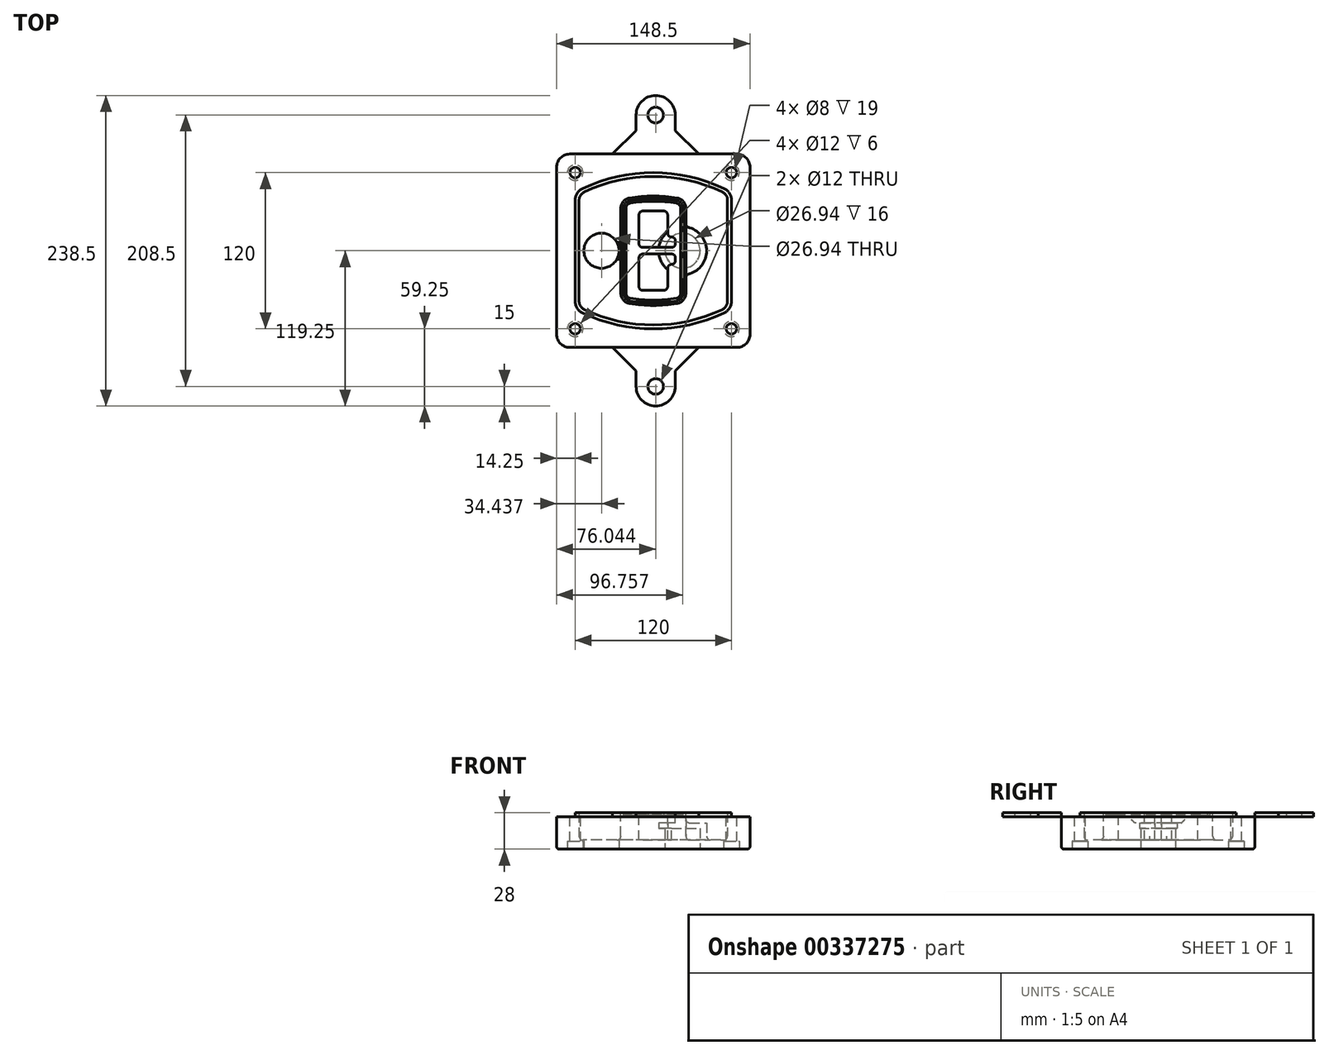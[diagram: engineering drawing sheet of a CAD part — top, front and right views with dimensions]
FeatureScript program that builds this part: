
annotation { "Feature Type Name" : "Feature", "Feature Type Description" : "" }
export const myFeature = defineFeature(function(context is Context, id is Id, definition is map)
    precondition{}
    {
        {
            var Q0;
            Q0=qCreatedBy(makeId("Top.planeOp"),FACE);
            var sketch = newSketch(context, id + "F0", { "sketchPlane" : qUnion([Q0])});
            skPoint(sketch, "E0.rect.middle", {"position": v(0, 0) * mm});
            skLineSegment(sketch, "E1.bottom", {"start": v(-64.25, -74.25) * mm, "end": v(64.25, -74.25) * mm});
            skLineSegment(sketch, "E1.top", {"start": v(-64.25, 74.25) * mm, "end": v(64.25, 74.25) * mm});
            skLineSegment(sketch, "E1.left", {"start": v(-74.25, -64.25) * mm, "end": v(-74.25, 64.25) * mm});
            skLineSegment(sketch, "E1.right", {"start": v(74.25, -64.25) * mm, "end": v(74.25, 64.25) * mm});
            skLineSegment(sketch, "E2", {"start": v(-74.25, 74.25) * mm, "end": v(74.25, -74.25) * mm, "construction": true});
            skLineSegment(sketch, "E3", {"start": v(74.25, 74.25) * mm, "end": v(-74.25, -74.25) * mm, "construction": true});
            skCircle(sketch, "E4", {"center": v(-60, 60) * mm, "radius": 4 * mm});
            skCircle(sketch, "E5", {"center": v(60, 60) * mm, "radius": 4 * mm});
            skCircle(sketch, "E6", {"center": v(60, -60) * mm, "radius": 4 * mm});
            skCircle(sketch, "E7", {"center": v(-60, -60) * mm, "radius": 4 * mm});
            skLineSegment(sketch, "E8", {"start": v(-60, 60) * mm, "end": v(60, 60) * mm, "construction": true});
            skLineSegment(sketch, "E9", {"start": v(60, 60) * mm, "end": v(60, -60) * mm, "construction": true});
            skLineSegment(sketch, "E10", {"start": v(60, -60) * mm, "end": v(-60, -60) * mm, "construction": true});
            skLineSegment(sketch, "E11", {"start": v(-60, -60) * mm, "end": v(-60, 60) * mm, "construction": true});
            skLineSegment(sketch, "E12", {"start": v(-60, 38.83) * mm, "end": v(-60, -38.83) * mm});
            skLineSegment(sketch, "E13", {"start": v(60, 38.83) * mm, "end": v(60, -38.83) * mm});
            skArc(sketch, "E14", {"start": v(54.26, 47.88) * mm, "mid": v(0, 60) * mm, "end": v(-54.26, 47.88) * mm});
            skArc(sketch, "E15", {"start": v(-54.26, -47.88) * mm, "mid": v(0, -60) * mm, "end": v(54.26, -47.88) * mm});
            skLineSegment(sketch, "E16", {"start": v(-60, 0) * mm, "end": v(60, 0) * mm, "construction": true});
            skPoint(sketch, "E17.visualSharp", {"position": v(-60, -45) * mm});
            skArc(sketch, "E17.filletArc", {"start": v(-60, -38.83) * mm, "mid": v(-58.44, -44.2) * mm, "end": v(-54.26, -47.88) * mm});
            skPoint(sketch, "E18.visualSharp", {"position": v(-60, 45) * mm});
            skArc(sketch, "E18.filletArc", {"start": v(-54.26, 47.88) * mm, "mid": v(-58.44, 44.2) * mm, "end": v(-60, 38.83) * mm});
            skPoint(sketch, "E19.visualSharp", {"position": v(60, 45) * mm});
            skArc(sketch, "E19.filletArc", {"start": v(60, 38.83) * mm, "mid": v(58.44, 44.2) * mm, "end": v(54.26, 47.88) * mm});
            skPoint(sketch, "E20.visualSharp", {"position": v(60, -45) * mm});
            skArc(sketch, "E20.filletArc", {"start": v(54.26, -47.88) * mm, "mid": v(58.44, -44.2) * mm, "end": v(60, -38.83) * mm});
            skPoint(sketch, "E21.visualSharp", {"position": v(-74.25, 74.25) * mm});
            skArc(sketch, "E21.filletArc", {"start": v(-64.25, 74.25) * mm, "mid": v(-71.32, 71.32) * mm, "end": v(-74.25, 64.25) * mm});
            skPoint(sketch, "E22.visualSharp", {"position": v(74.25, 74.25) * mm});
            skArc(sketch, "E22.filletArc", {"start": v(74.25, 64.25) * mm, "mid": v(71.32, 71.32) * mm, "end": v(64.25, 74.25) * mm});
            skPoint(sketch, "E23.visualSharp", {"position": v(74.25, -74.25) * mm});
            skArc(sketch, "E23.filletArc", {"start": v(64.25, -74.25) * mm, "mid": v(71.32, -71.32) * mm, "end": v(74.25, -64.25) * mm});
            skPoint(sketch, "E24.visualSharp", {"position": v(-74.25, -74.25) * mm});
            skArc(sketch, "E24.filletArc", {"start": v(-74.25, -64.25) * mm, "mid": v(-71.32, -71.32) * mm, "end": v(-64.25, -74.25) * mm});
            skArc(sketch, "E25.0", {"start": v(57, 38.83) * mm, "mid": v(55.9, 42.58) * mm, "end": v(52.98, 45.17) * mm});
            skLineSegment(sketch, "E25.1", {"start": v(57, 38.83) * mm, "end": v(57, -38.83) * mm});
            skArc(sketch, "E25.2", {"start": v(52.98, -45.17) * mm, "mid": v(55.9, -42.58) * mm, "end": v(57, -38.83) * mm});
            skArc(sketch, "E25.3", {"start": v(-52.98, -45.17) * mm, "mid": v(0, -57) * mm, "end": v(52.98, -45.17) * mm});
            skArc(sketch, "E25.4", {"start": v(-57, -38.83) * mm, "mid": v(-55.9, -42.58) * mm, "end": v(-52.98, -45.17) * mm});
            skArc(sketch, "E25.5", {"start": v(52.98, 45.17) * mm, "mid": v(0, 57) * mm, "end": v(-52.98, 45.17) * mm});
            skLineSegment(sketch, "E25.6", {"start": v(-57, 38.83) * mm, "end": v(-57, -38.83) * mm});
            skArc(sketch, "E25.7", {"start": v(-52.98, 45.17) * mm, "mid": v(-55.9, 42.58) * mm, "end": v(-57, 38.83) * mm});
            skArc(sketch, "E26.0", {"start": v(-55.96, 51.5) * mm, "mid": v(-61.82, 46.33) * mm, "end": v(-64, 38.83) * mm});
            skArc(sketch, "E26.1", {"start": v(55.96, 51.5) * mm, "mid": v(0, 64) * mm, "end": v(-55.96, 51.5) * mm});
            skArc(sketch, "E26.2", {"start": v(64, 38.83) * mm, "mid": v(61.82, 46.33) * mm, "end": v(55.96, 51.5) * mm});
            skLineSegment(sketch, "E26.3", {"start": v(64, 38.83) * mm, "end": v(64, -38.83) * mm});
            skArc(sketch, "E26.4", {"start": v(55.96, -51.5) * mm, "mid": v(61.82, -46.33) * mm, "end": v(64, -38.83) * mm});
            skLineSegment(sketch, "E26.5", {"start": v(-64, 38.83) * mm, "end": v(-64, -38.83) * mm});
            skArc(sketch, "E26.6", {"start": v(-55.96, -51.5) * mm, "mid": v(0, -64) * mm, "end": v(55.96, -51.5) * mm});
            skArc(sketch, "E26.7", {"start": v(-64, -38.83) * mm, "mid": v(-61.82, -46.33) * mm, "end": v(-55.96, -51.5) * mm});
            skSolve(sketch);
        }
        {
            var Q0;
            Q0=makeQuery(id+"F0.imprint","IMPRINT",FACE,{"disambiguationData":[TD([[makeQuery(id+"F0.imprint","IMPRINT",EDGE,{"derivedFrom":sQuery(id+"F0.wireOp",EDGE,"E1.bottom")}),1.0]])]});
            var Q1;
            Q1=makeQuery(id+"F0.imprint","IMPRINT",FACE,{"disambiguationData":[TD([[makeQuery(id+"F0.imprint","IMPRINT",EDGE,{"derivedFrom":sQuery(id+"F0.wireOp",EDGE,"E12")}),1.0]])]});
            var Q2;
            Q2=makeQuery(id+"F0.imprint","IMPRINT",FACE,{"disambiguationData":[TD([[makeQuery(id+"F0.imprint","IMPRINT",EDGE,{"derivedFrom":sQuery(id+"F0.wireOp",EDGE,"E25.0")}),1.0]])]});
            var Q3;
            Q3=makeQuery(id+"F0.imprint","IMPRINT",FACE,{"disambiguationData":[TD([[makeQuery(id+"F0.imprint","IMPRINT",EDGE,{"derivedFrom":sQuery(id+"F0.wireOp",EDGE,"E12")}),-1.0]])]});
            extrude(context, id + "F1", {"entities" : qUnion([Q0, Q1, Q2, Q3]), "oppositeDirection" : true, "depth" : 25 * mm});
        }
        {
            var Q0;
            Q0=makeQuery(id+"F0.imprint","IMPRINT",FACE,{"disambiguationData":[TD([[makeQuery(id+"F0.imprint","IMPRINT",EDGE,{"derivedFrom":sQuery(id+"F0.wireOp",EDGE,"E12")}),1.0]])]});
            extrude(context, id + "F2", {"entities" : qUnion([Q0]), "operationType" : NewBodyOperationType.ADD, "depth" : 3 * mm});
        }
        {
            var Q0;
            Q0=makeQuery(id+"F0.imprint","IMPRINT",FACE,{"disambiguationData":[TD([[makeQuery(id+"F0.imprint","IMPRINT",EDGE,{"derivedFrom":sQuery(id+"F0.wireOp",EDGE,"E25.0")}),1.0]])]});
            extrude(context, id + "F3", {"entities" : qUnion([Q0]), "operationType" : NewBodyOperationType.REMOVE, "oppositeDirection" : true, "depth" : 18 * mm});
        }
        {
            var Q0;
            Q0=makeQuery(id+"F2.opExtrude","CAP_FACE",FACE,{"disambiguationData":[OSD([sQuery(id+"F0.wireOp",EDGE,"E12"),sQuery(id+"F0.wireOp",EDGE,"E13"),sQuery(id+"F0.wireOp",EDGE,"E14"),sQuery(id+"F0.wireOp",EDGE,"E15"),sQuery(id+"F0.wireOp",EDGE,"E17.filletArc"),sQuery(id+"F0.wireOp",EDGE,"E18.filletArc"),sQuery(id+"F0.wireOp",EDGE,"E19.filletArc"),sQuery(id+"F0.wireOp",EDGE,"E20.filletArc"),sQuery(id+"F0.wireOp",EDGE,"E25.0"),sQuery(id+"F0.wireOp",EDGE,"E25.1"),sQuery(id+"F0.wireOp",EDGE,"E25.2"),sQuery(id+"F0.wireOp",EDGE,"E25.3"),sQuery(id+"F0.wireOp",EDGE,"E25.4"),sQuery(id+"F0.wireOp",EDGE,"E25.5"),sQuery(id+"F0.wireOp",EDGE,"E25.6"),sQuery(id+"F0.wireOp",EDGE,"E25.7")])],"isStart":false});
            var sketch = newSketch(context, id + "F4", { "sketchPlane" : qUnion([Q0])});
            skArc(sketch, "E27.0", {"start": v(-18.34, -40.45) * mm, "mid": v(0, -42) * mm, "end": v(18.34, -40.45) * mm});
            skArc(sketch, "E28.0", {"start": v(18.34, 40.45) * mm, "mid": v(0, 42) * mm, "end": v(-18.34, 40.45) * mm});
            skLineSegment(sketch, "E29", {"start": v(-25, 32.57) * mm, "end": v(-25, -32.57) * mm});
            skLineSegment(sketch, "E30", {"start": v(25, 32.57) * mm, "end": v(25, -32.57) * mm});
            skLineSegment(sketch, "E31", {"start": v(-25, 39.1) * mm, "end": v(25, 39.1) * mm, "construction": true});
            skLineSegment(sketch, "E32", {"start": v(-25, -39.1) * mm, "end": v(25, -39.1) * mm, "construction": true});
            skPoint(sketch, "E33.visualSharp", {"position": v(-25, 39.1) * mm});
            skArc(sketch, "E33.filletArc", {"start": v(-18.34, 40.45) * mm, "mid": v(-23.11, 37.73) * mm, "end": v(-25, 32.57) * mm});
            skPoint(sketch, "E34.visualSharp", {"position": v(25, 39.1) * mm});
            skArc(sketch, "E34.filletArc", {"start": v(25, 32.57) * mm, "mid": v(23.11, 37.73) * mm, "end": v(18.34, 40.45) * mm});
            skPoint(sketch, "E35.visualSharp", {"position": v(25, -39.1) * mm});
            skArc(sketch, "E35.filletArc", {"start": v(18.34, -40.45) * mm, "mid": v(23.11, -37.73) * mm, "end": v(25, -32.57) * mm});
            skPoint(sketch, "E36.visualSharp", {"position": v(-25, -39.1) * mm});
            skArc(sketch, "E36.filletArc", {"start": v(-25, -32.57) * mm, "mid": v(-23.11, -37.73) * mm, "end": v(-18.34, -40.45) * mm});
            skArc(sketch, "E37.0", {"start": v(52.98, 45.17) * mm, "mid": v(0, 57) * mm, "end": v(-52.98, 45.17) * mm});
            skArc(sketch, "E37.1", {"start": v(-52.98, 45.17) * mm, "mid": v(-55.9, 42.58) * mm, "end": v(-57, 38.83) * mm});
            skLineSegment(sketch, "E37.2", {"start": v(-57, 38.83) * mm, "end": v(-57, -38.83) * mm});
            skArc(sketch, "E37.3", {"start": v(-57, -38.83) * mm, "mid": v(-55.9, -42.58) * mm, "end": v(-52.98, -45.17) * mm});
            skArc(sketch, "E37.4", {"start": v(-52.98, -45.17) * mm, "mid": v(0, -57) * mm, "end": v(52.98, -45.17) * mm});
            skArc(sketch, "E37.5", {"start": v(52.98, -45.17) * mm, "mid": v(55.9, -42.58) * mm, "end": v(57, -38.83) * mm});
            skLineSegment(sketch, "E37.6", {"start": v(57, 38.83) * mm, "end": v(57, -38.83) * mm});
            skArc(sketch, "E37.7", {"start": v(57, 38.83) * mm, "mid": v(55.9, 42.58) * mm, "end": v(52.98, 45.17) * mm});
            skLineSegment(sketch, "E38.0", {"start": v(23, 32.57) * mm, "end": v(23, -32.57) * mm});
            skArc(sketch, "E38.1", {"start": v(18, -38.48) * mm, "mid": v(21.58, -36.44) * mm, "end": v(23, -32.57) * mm});
            skArc(sketch, "E38.2", {"start": v(-18, -38.48) * mm, "mid": v(0, -40) * mm, "end": v(18, -38.48) * mm});
            skArc(sketch, "E38.3", {"start": v(-23, -32.57) * mm, "mid": v(-21.58, -36.44) * mm, "end": v(-18, -38.48) * mm});
            skLineSegment(sketch, "E38.4", {"start": v(-23, 32.57) * mm, "end": v(-23, -32.57) * mm});
            skArc(sketch, "E38.5", {"start": v(23, 32.57) * mm, "mid": v(21.58, 36.44) * mm, "end": v(18, 38.48) * mm});
            skArc(sketch, "E38.6", {"start": v(-18, 38.48) * mm, "mid": v(-21.58, 36.44) * mm, "end": v(-23, 32.57) * mm});
            skArc(sketch, "E38.7", {"start": v(18, 38.48) * mm, "mid": v(0, 40) * mm, "end": v(-18, 38.48) * mm});
            skArc(sketch, "E39.0", {"start": v(21, 32.57) * mm, "mid": v(20.06, 35.15) * mm, "end": v(17.67, 36.5) * mm});
            skLineSegment(sketch, "E39.1", {"start": v(21, 32.57) * mm, "end": v(21, -32.57) * mm});
            skArc(sketch, "E39.2", {"start": v(17.67, -36.5) * mm, "mid": v(20.06, -35.15) * mm, "end": v(21, -32.57) * mm});
            skArc(sketch, "E39.3", {"start": v(-17.67, -36.5) * mm, "mid": v(0, -38) * mm, "end": v(17.67, -36.5) * mm});
            skArc(sketch, "E39.4", {"start": v(-21, -32.57) * mm, "mid": v(-20.06, -35.15) * mm, "end": v(-17.67, -36.5) * mm});
            skArc(sketch, "E39.5", {"start": v(17.67, 36.5) * mm, "mid": v(0, 38) * mm, "end": v(-17.67, 36.5) * mm});
            skLineSegment(sketch, "E39.6", {"start": v(-21, 32.57) * mm, "end": v(-21, -32.57) * mm});
            skArc(sketch, "E39.7", {"start": v(-17.67, 36.5) * mm, "mid": v(-20.06, 35.15) * mm, "end": v(-21, 32.57) * mm});
            skLineSegment(sketch, "E40", {"start": v(-25, 0) * mm, "end": v(25, 0) * mm, "construction": true});
            skLineSegment(sketch, "E41", {"start": v(-11, 5.5) * mm, "end": v(-11, 27.5) * mm});
            skLineSegment(sketch, "E42", {"start": v(-8, 30.5) * mm, "end": v(8, 30.5) * mm});
            skLineSegment(sketch, "E43", {"start": v(11, 27.5) * mm, "end": v(11, 13.5) * mm});
            skLineSegment(sketch, "E44", {"start": v(14, 10.5) * mm, "end": v(14, 10.5) * mm});
            skLineSegment(sketch, "E45", {"start": v(17, 7.5) * mm, "end": v(17, 5.5) * mm});
            skLineSegment(sketch, "E46", {"start": v(14, 2.5) * mm, "end": v(-8, 2.5) * mm});
            skPoint(sketch, "E47.visualSharp", {"position": v(-11, 30.5) * mm});
            skArc(sketch, "E47.filletArc", {"start": v(-8, 30.5) * mm, "mid": v(-10.12, 29.62) * mm, "end": v(-11, 27.5) * mm});
            skPoint(sketch, "E48.visualSharp", {"position": v(11, 30.5) * mm});
            skArc(sketch, "E48.filletArc", {"start": v(11, 27.5) * mm, "mid": v(10.12, 29.62) * mm, "end": v(8, 30.5) * mm});
            skPoint(sketch, "E49.visualSharp", {"position": v(11, 10.5) * mm});
            skArc(sketch, "E49.filletArc", {"start": v(11, 13.5) * mm, "mid": v(11.88, 11.38) * mm, "end": v(14, 10.5) * mm});
            skPoint(sketch, "E50.visualSharp", {"position": v(17, 10.5) * mm});
            skArc(sketch, "E50.filletArc", {"start": v(17, 7.5) * mm, "mid": v(16.12, 9.62) * mm, "end": v(14, 10.5) * mm});
            skPoint(sketch, "E51.visualSharp", {"position": v(17, 2.5) * mm});
            skArc(sketch, "E51.filletArc", {"start": v(14, 2.5) * mm, "mid": v(16.12, 3.38) * mm, "end": v(17, 5.5) * mm});
            skPoint(sketch, "E52.visualSharp", {"position": v(-11, 2.5) * mm});
            skArc(sketch, "E52.filletArc", {"start": v(-11, 5.5) * mm, "mid": v(-10.12, 3.38) * mm, "end": v(-8, 2.5) * mm});
            skLineSegment(sketch, "E53.0.MirrorCS", {"start": v(14, -2.5) * mm, "end": v(-8, -2.5) * mm});
            skArc(sketch, "E54.0.MirrorCS", {"start": v(-11, -5.5) * mm, "mid": v(-10.12, -3.38) * mm, "end": v(-8, -2.5) * mm});
            skLineSegment(sketch, "E55.0.MirrorCS", {"start": v(-11, -5.5) * mm, "end": v(-11, -27.5) * mm});
            skArc(sketch, "E56.0.MirrorCS", {"start": v(-8, -30.5) * mm, "mid": v(-10.12, -29.62) * mm, "end": v(-11, -27.5) * mm});
            skLineSegment(sketch, "E57.0.MirrorCS", {"start": v(-8, -30.5) * mm, "end": v(8, -30.5) * mm});
            skArc(sketch, "E58.0.MirrorCS", {"start": v(11, -27.5) * mm, "mid": v(10.12, -29.62) * mm, "end": v(8, -30.5) * mm});
            skLineSegment(sketch, "E59.0.MirrorCS", {"start": v(11, -27.5) * mm, "end": v(11, -13.5) * mm});
            skArc(sketch, "E60.0.MirrorCS", {"start": v(11, -13.5) * mm, "mid": v(11.88, -11.38) * mm, "end": v(14, -10.5) * mm});
            skArc(sketch, "E61.0.MirrorCS", {"start": v(17, -7.5) * mm, "mid": v(16.12, -9.62) * mm, "end": v(14, -10.5) * mm});
            skLineSegment(sketch, "E62.0.MirrorCS", {"start": v(17, -7.5) * mm, "end": v(17, -5.5) * mm});
            skArc(sketch, "E63.0.MirrorCS", {"start": v(14, -2.5) * mm, "mid": v(16.12, -3.38) * mm, "end": v(17, -5.5) * mm});
            skSolve(sketch);
        }
        {
            var Q0;
            Q0=makeQuery(id+"F4.imprint","IMPRINT",FACE,{"disambiguationData":[TD([[makeQuery(id+"F4.imprint","IMPRINT",EDGE,{"derivedFrom":sQuery(id+"F4.wireOp",EDGE,"E27.0")}),1.0]])]});
            var Q1;
            Q1=makeQuery(id+"F4.imprint","IMPRINT",FACE,{"disambiguationData":[TD([[makeQuery(id+"F4.imprint","IMPRINT",EDGE,{"derivedFrom":sQuery(id+"F4.wireOp",EDGE,"E38.0")}),-1.0]])]});
            var Q2;
            Q2=makeQuery(id+"F4.imprint","IMPRINT",FACE,{"disambiguationData":[TD([[makeQuery(id+"F4.imprint","IMPRINT",EDGE,{"derivedFrom":sQuery(id+"F4.wireOp",EDGE,"E39.0")}),1.0]])]});
            extrude(context, id + "F5", {"entities" : qUnion([Q0, Q1, Q2]), "operationType" : NewBodyOperationType.ADD, "endBound" : BoundingType.UP_TO_NEXT, "oppositeDirection" : true, "depth" : 25 * mm});
        }
        {
            var Q0;
            Q0=makeQuery(id+"F4.imprint","IMPRINT",FACE,{"disambiguationData":[TD([[makeQuery(id+"F4.imprint","IMPRINT",EDGE,{"derivedFrom":sQuery(id+"F4.wireOp",EDGE,"E38.0")}),-1.0]])]});
            extrude(context, id + "F6", {"entities" : qUnion([Q0]), "operationType" : NewBodyOperationType.REMOVE, "oppositeDirection" : true, "depth" : 2 * mm});
        }
        {
            var Q0;
            Q0=makeQuery(id+"F1.opExtrude","CAP_FACE",FACE,{"disambiguationData":[OSD([sQuery(id+"F0.wireOp",EDGE,"E1.bottom"),sQuery(id+"F0.wireOp",EDGE,"E1.top"),sQuery(id+"F0.wireOp",EDGE,"E1.left"),sQuery(id+"F0.wireOp",EDGE,"E1.right"),sQuery(id+"F0.wireOp",EDGE,"E4"),sQuery(id+"F0.wireOp",EDGE,"E5"),sQuery(id+"F0.wireOp",EDGE,"E6"),sQuery(id+"F0.wireOp",EDGE,"E7"),sQuery(id+"F0.wireOp",EDGE,"E21.filletArc"),sQuery(id+"F0.wireOp",EDGE,"E22.filletArc"),sQuery(id+"F0.wireOp",EDGE,"E23.filletArc"),sQuery(id+"F0.wireOp",EDGE,"E24.filletArc")])],"isStart":false});
            var sketch = newSketch(context, id + "F7", { "sketchPlane" : qUnion([Q0])});
            skCircle(sketch, "E64", {"center": v(22.5, 0) * mm, "radius": 13.47 * mm});
            skCircle(sketch, "E65", {"center": v(-39.81, 0) * mm, "radius": 13.47 * mm});
            skLineSegment(sketch, "E66", {"start": v(74.25, 0) * mm, "end": v(-74.25, 0) * mm});
            skCircle(sketch, "E67", {"center": v(22.5, 0) * mm, "radius": 18.47 * mm});
            skCircle(sketch, "E68", {"center": v(60, -60) * mm, "radius": 6 * mm});
            skCircle(sketch, "E69", {"center": v(-60, -60) * mm, "radius": 6 * mm});
            skCircle(sketch, "E70", {"center": v(-60, 60) * mm, "radius": 6 * mm});
            skCircle(sketch, "E71", {"center": v(60, 60) * mm, "radius": 6 * mm});
            skSolve(sketch);
        }
        {
            var Q0;
            {var subQ1=sQuery(id+"F7.wireOp",EDGE,"E66");var subQ4=sQuery(id+"F7.wireOp",EDGE,"E64");var subQ6=makeQuery(id+"F7.imprint","INTERSECT",VERTEX,{"disambiguationData":[OD(0.0)],"derivedFrom":[subQ4,subQ1]});Q0=makeQuery(id+"F7.imprint","IMPRINT",FACE,{"disambiguationData":[TD([[makeQuery(id+"F7.imprint","IMPRINT",EDGE,{"disambiguationData":[TD([[subQ6,-1.0]])],"derivedFrom":subQ4}),-1.0]])]});}
            var Q1;
            {var subQ0=sQuery(id+"F7.wireOp",EDGE,"E66");var subQ1=sQuery(id+"F7.wireOp",EDGE,"E64");var subQ3=makeQuery(id+"F7.imprint","INTERSECT",VERTEX,{"disambiguationData":[OD(0.0)],"derivedFrom":[subQ1,subQ0]});Q1=makeQuery(id+"F7.imprint","IMPRINT",FACE,{"disambiguationData":[TD([[makeQuery(id+"F7.imprint","IMPRINT",EDGE,{"disambiguationData":[TD([[subQ3,-1.0]])],"derivedFrom":subQ1}),1.0]])]});}
            var Q2;
            {var subQ0=sQuery(id+"F7.wireOp",EDGE,"E66");var subQ1=sQuery(id+"F7.wireOp",EDGE,"E64");var subQ3=makeQuery(id+"F7.imprint","INTERSECT",VERTEX,{"disambiguationData":[OD(0.0)],"derivedFrom":[subQ1,subQ0]});Q2=makeQuery(id+"F7.imprint","IMPRINT",FACE,{"disambiguationData":[TD([[makeQuery(id+"F7.imprint","IMPRINT",EDGE,{"disambiguationData":[TD([[subQ3,1.0]])],"derivedFrom":subQ1}),1.0]])]});}
            var Q3;
            {var subQ1=sQuery(id+"F7.wireOp",EDGE,"E66");var subQ4=sQuery(id+"F7.wireOp",EDGE,"E64");var subQ6=makeQuery(id+"F7.imprint","INTERSECT",VERTEX,{"disambiguationData":[OD(0.0)],"derivedFrom":[subQ4,subQ1]});Q3=makeQuery(id+"F7.imprint","IMPRINT",FACE,{"disambiguationData":[TD([[makeQuery(id+"F7.imprint","IMPRINT",EDGE,{"disambiguationData":[TD([[subQ6,1.0]])],"derivedFrom":subQ4}),-1.0]])]});}
            extrude(context, id + "F8", {"entities" : qUnion([Q0, Q1, Q2, Q3]), "operationType" : NewBodyOperationType.ADD, "oppositeDirection" : true, "depth" : 20 * mm});
        }
        {
            var Q0;
            {var subQ0=sQuery(id+"F7.wireOp",EDGE,"E66");var subQ1=sQuery(id+"F7.wireOp",EDGE,"E64");var subQ3=makeQuery(id+"F7.imprint","INTERSECT",VERTEX,{"disambiguationData":[OD(0.0)],"derivedFrom":[subQ1,subQ0]});Q0=makeQuery(id+"F7.imprint","IMPRINT",FACE,{"disambiguationData":[TD([[makeQuery(id+"F7.imprint","IMPRINT",EDGE,{"disambiguationData":[TD([[subQ3,-1.0]])],"derivedFrom":subQ1}),1.0]])]});}
            var Q1;
            {var subQ0=sQuery(id+"F7.wireOp",EDGE,"E66");var subQ1=sQuery(id+"F7.wireOp",EDGE,"E64");var subQ3=makeQuery(id+"F7.imprint","INTERSECT",VERTEX,{"disambiguationData":[OD(0.0)],"derivedFrom":[subQ1,subQ0]});Q1=makeQuery(id+"F7.imprint","IMPRINT",FACE,{"disambiguationData":[TD([[makeQuery(id+"F7.imprint","IMPRINT",EDGE,{"disambiguationData":[TD([[subQ3,1.0]])],"derivedFrom":subQ1}),1.0]])]});}
            extrude(context, id + "F9", {"entities" : qUnion([Q0, Q1]), "operationType" : NewBodyOperationType.REMOVE, "oppositeDirection" : true, "depth" : 16 * mm});
        }
        {
            var Q0;
            {var subQ0=sQuery(id+"F7.wireOp",EDGE,"E66");var subQ1=sQuery(id+"F7.wireOp",EDGE,"E65");var subQ3=makeQuery(id+"F7.imprint","INTERSECT",VERTEX,{"disambiguationData":[OD(0.0)],"derivedFrom":[subQ1,subQ0]});Q0=makeQuery(id+"F7.imprint","IMPRINT",FACE,{"disambiguationData":[TD([[makeQuery(id+"F7.imprint","IMPRINT",EDGE,{"disambiguationData":[TD([[subQ3,-1.0]])],"derivedFrom":subQ1}),1.0]])]});}
            var Q1;
            {var subQ0=sQuery(id+"F7.wireOp",EDGE,"E66");var subQ1=sQuery(id+"F7.wireOp",EDGE,"E65");var subQ3=makeQuery(id+"F7.imprint","INTERSECT",VERTEX,{"disambiguationData":[OD(0.0)],"derivedFrom":[subQ1,subQ0]});Q1=makeQuery(id+"F7.imprint","IMPRINT",FACE,{"disambiguationData":[TD([[makeQuery(id+"F7.imprint","IMPRINT",EDGE,{"disambiguationData":[TD([[subQ3,1.0]])],"derivedFrom":subQ1}),1.0]])]});}
            extrude(context, id + "F10", {"entities" : qUnion([Q0, Q1]), "operationType" : NewBodyOperationType.REMOVE, "oppositeDirection" : true, "depth" : 25 * mm});
        }
        {
            var Q0;
            Q0=makeQuery(id+"F7.imprint","IMPRINT",FACE,{"disambiguationData":[TD([[makeQuery(id+"F7.imprint","IMPRINT",EDGE,{"derivedFrom":sQuery(id+"F7.wireOp",EDGE,"E68")}),1.0]])]});
            var Q1;
            Q1=makeQuery(id+"F7.imprint","IMPRINT",FACE,{"disambiguationData":[TD([[makeQuery(id+"F7.imprint","IMPRINT",EDGE,{"derivedFrom":makeQuery(id+"F1.opExtrude","CAP_EDGE",EDGE,{"disambiguationData":[OSD([sQuery(id+"F0.wireOp",EDGE,"E5")])],"isStart":false})}),-1.0]])]});
            var Q2;
            Q2=makeQuery(id+"F7.imprint","IMPRINT",FACE,{"disambiguationData":[TD([[makeQuery(id+"F7.imprint","IMPRINT",EDGE,{"derivedFrom":sQuery(id+"F7.wireOp",EDGE,"E69")}),1.0]])]});
            var Q3;
            Q3=makeQuery(id+"F7.imprint","IMPRINT",FACE,{"disambiguationData":[TD([[makeQuery(id+"F7.imprint","IMPRINT",EDGE,{"derivedFrom":makeQuery(id+"F1.opExtrude","CAP_EDGE",EDGE,{"disambiguationData":[OSD([sQuery(id+"F0.wireOp",EDGE,"E4")])],"isStart":false})}),-1.0]])]});
            var Q4;
            Q4=makeQuery(id+"F7.imprint","IMPRINT",FACE,{"disambiguationData":[TD([[makeQuery(id+"F7.imprint","IMPRINT",EDGE,{"derivedFrom":sQuery(id+"F7.wireOp",EDGE,"E70")}),1.0]])]});
            var Q5;
            Q5=makeQuery(id+"F7.imprint","IMPRINT",FACE,{"disambiguationData":[TD([[makeQuery(id+"F7.imprint","IMPRINT",EDGE,{"derivedFrom":makeQuery(id+"F1.opExtrude","CAP_EDGE",EDGE,{"disambiguationData":[OSD([sQuery(id+"F0.wireOp",EDGE,"E7")])],"isStart":false})}),-1.0]])]});
            var Q6;
            Q6=makeQuery(id+"F7.imprint","IMPRINT",FACE,{"disambiguationData":[TD([[makeQuery(id+"F7.imprint","IMPRINT",EDGE,{"derivedFrom":sQuery(id+"F7.wireOp",EDGE,"E71")}),1.0]])]});
            var Q7;
            Q7=makeQuery(id+"F7.imprint","IMPRINT",FACE,{"disambiguationData":[TD([[makeQuery(id+"F7.imprint","IMPRINT",EDGE,{"derivedFrom":makeQuery(id+"F1.opExtrude","CAP_EDGE",EDGE,{"disambiguationData":[OSD([sQuery(id+"F0.wireOp",EDGE,"E6")])],"isStart":false})}),-1.0]])]});
            extrude(context, id + "F11", {"entities" : qUnion([Q0, Q1, Q2, Q3, Q4, Q5, Q6, Q7]), "operationType" : NewBodyOperationType.REMOVE, "oppositeDirection" : true, "depth" : 6 * mm});
        }
        {
            var Q0;
            Q0=makeQuery(id+"F9.boolean.opBoolean","COPY",FACE,{"derivedFrom":makeQuery(id+"F9.opExtrude","CAP_FACE",FACE,{"disambiguationData":[OSD([sQuery(id+"F7.wireOp",EDGE,"E64")])],"isStart":false})});
            var sketch = newSketch(context, id + "F12", { "sketchPlane" : qUnion([Q0])});
            skArc(sketch, "E72.0", {"start": v(11, 14.45) * mm, "mid": v(6.45, 9.13) * mm, "end": v(4.2, 2.5) * mm});
            skArc(sketch, "E72.1", {"start": v(4.2, -2.5) * mm, "mid": v(6.45, -9.13) * mm, "end": v(11, -14.45) * mm});
            skLineSegment(sketch, "E73", {"start": v(4.2, -2.5) * mm, "end": v(14, -2.5) * mm});
            skLineSegment(sketch, "E74.0", {"start": v(14, 2.5) * mm, "end": v(4.2, 2.5) * mm});
            skArc(sketch, "E74.1", {"start": v(14, 2.5) * mm, "mid": v(16.12, 3.38) * mm, "end": v(17, 5.5) * mm});
            skLineSegment(sketch, "E74.2", {"start": v(17, 7.5) * mm, "end": v(17, 5.5) * mm});
            skArc(sketch, "E74.3", {"start": v(17, 7.5) * mm, "mid": v(16.12, 9.62) * mm, "end": v(14, 10.5) * mm});
            skArc(sketch, "E74.4", {"start": v(11, 13.5) * mm, "mid": v(11.88, 11.38) * mm, "end": v(14, 10.5) * mm});
            skLineSegment(sketch, "E74.5", {"start": v(11, 14.45) * mm, "end": v(11, 13.5) * mm});
            skLineSegment(sketch, "E74.7", {"start": v(14, -2.5) * mm, "end": v(4.2, -2.5) * mm});
            skArc(sketch, "E74.8", {"start": v(14, -2.5) * mm, "mid": v(16.12, -3.38) * mm, "end": v(17, -5.5) * mm});
            skLineSegment(sketch, "E74.9", {"start": v(17, -7.5) * mm, "end": v(17, -5.5) * mm});
            skArc(sketch, "E74.10", {"start": v(17, -7.5) * mm, "mid": v(16.12, -9.62) * mm, "end": v(14, -10.5) * mm});
            skArc(sketch, "E74.11", {"start": v(11, -13.5) * mm, "mid": v(11.88, -11.38) * mm, "end": v(14, -10.5) * mm});
            skLineSegment(sketch, "E74.12", {"start": v(11, -14.45) * mm, "end": v(11, -13.5) * mm});
            skPoint(sketch, "E75.orphan", {"position": v(11, -27.5) * mm});
            skPoint(sketch, "E76.orphan", {"position": v(-8, -2.5) * mm});
            skPoint(sketch, "E77.orphan", {"position": v(-8, 2.5) * mm});
            skPoint(sketch, "E78.orphan", {"position": v(11, 27.5) * mm});
            skSolve(sketch);
        }
        {
            var Q0;
            {var subQ7=sQuery(id+"F12.wireOp",EDGE,"E72.0");var subQ14=sQuery(id+"F12.wireOp",EDGE,"E72.1");var subQ16=sQuery(id+"F12.wireOp",EDGE,"E74.1");var subQ18=sQuery(id+"F12.wireOp",EDGE,"E74.8");Q0=qUnion([makeQuery(id+"F12.imprint","IMPRINT",FACE,{"disambiguationData":[TD([[makeQuery(id+"F12.imprint","IMPRINT",EDGE,{"derivedFrom":subQ7}),1.0]])]}),makeQuery(id+"F12.imprint","IMPRINT",FACE,{"disambiguationData":[TD([[makeQuery(id+"F12.imprint","IMPRINT",EDGE,{"derivedFrom":subQ14}),1.0]])]}),makeQuery(id+"F12.imprint","IMPRINT",FACE,{"disambiguationData":[TD([[makeQuery(id+"F12.imprint","IMPRINT",EDGE,{"derivedFrom":subQ16}),1.0]])]}),makeQuery(id+"F12.imprint","IMPRINT",FACE,{"disambiguationData":[TD([[makeQuery(id+"F12.imprint","IMPRINT",EDGE,{"derivedFrom":subQ18}),-1.0]])]})]);}
            var Q1;
            Q1=makeQuery(id+"F5.boolean.opBoolean","SPLIT",FACE,{"disambiguationData":[TD([makeQuery(id+"F5.opExtrude","SWEPT_FACE",FACE,{"disambiguationData":[OSD([sQuery(id+"F4.wireOp",EDGE,"E41")])]})])],"derivedFrom":makeQuery(id+"F3.boolean.opBoolean","COPY",FACE,{"derivedFrom":makeQuery(id+"F3.opExtrude","CAP_FACE",FACE,{"disambiguationData":[OSD([sQuery(id+"F0.wireOp",EDGE,"E25.0"),sQuery(id+"F0.wireOp",EDGE,"E25.1"),sQuery(id+"F0.wireOp",EDGE,"E25.2"),sQuery(id+"F0.wireOp",EDGE,"E25.3"),sQuery(id+"F0.wireOp",EDGE,"E25.4"),sQuery(id+"F0.wireOp",EDGE,"E25.5"),sQuery(id+"F0.wireOp",EDGE,"E25.6"),sQuery(id+"F0.wireOp",EDGE,"E25.7")])],"isStart":false})})});
            extrude(context, id + "F13", {"entities" : qUnion([Q0]), "operationType" : NewBodyOperationType.REMOVE, "endBound" : BoundingType.UP_TO_SURFACE, "endBoundEntityFace" : qUnion([Q1]), "depth" : 25 * mm});
        }
        {
            var Q0;
            Q0=makeQuery(id+"F3.boolean.opBoolean","COPY",EDGE,{"derivedFrom":makeQuery(id+"F3.opExtrude","CAP_EDGE",EDGE,{"disambiguationData":[OSD([sQuery(id+"F0.wireOp",EDGE,"E25.6")])],"isStart":false})});
            var Q1;
            Q1=makeQuery(id+"F8.boolean.opBoolean","INTERSECT",EDGE,{"derivedFrom":[makeQuery(id+"F5.opExtrude","SWEPT_FACE",FACE,{"disambiguationData":[OSD([sQuery(id+"F4.wireOp",EDGE,"E30")])]}),makeQuery(id+"F8.opExtrude","CAP_FACE",FACE,{"disambiguationData":[OSD([sQuery(id+"F7.wireOp",EDGE,"E67")])],"isStart":false})]});
            var Q2;
            Q2=makeQuery(id+"F8.boolean.opBoolean","INTERSECT",EDGE,{"disambiguationData":[OD(1.0)],"derivedFrom":[makeQuery(id+"F5.opExtrude","SWEPT_FACE",FACE,{"disambiguationData":[OSD([sQuery(id+"F4.wireOp",EDGE,"E30")])]}),makeQuery(id+"F8.opExtrude","SWEPT_FACE",FACE,{"disambiguationData":[OSD([sQuery(id+"F7.wireOp",EDGE,"E67")])]})]});
            var Q3;
            {var subQ0=sQuery(id+"F4.wireOp",EDGE,"E30");Q3=makeQuery(id+"F8.boolean.opBoolean","SPLIT",EDGE,{"disambiguationData":[TD([makeQuery(id+"F5.opExtrude","SWEPT_FACE",FACE,{"disambiguationData":[OSD([sQuery(id+"F4.wireOp",EDGE,"E35.filletArc")])]})])],"derivedFrom":makeQuery(id+"F5.opExtrude","CAP_EDGE",EDGE,{"disambiguationData":[OSD([subQ0])],"isStart":false})});}
            var Q4;
            {var subQ0=sQuery(id+"F0.wireOp",EDGE,"E25.7");var subQ1=sQuery(id+"F0.wireOp",EDGE,"E25.1");var subQ2=sQuery(id+"F0.wireOp",EDGE,"E25.6");var subQ3=sQuery(id+"F0.wireOp",EDGE,"E25.5");var subQ4=sQuery(id+"F0.wireOp",EDGE,"E25.4");var subQ5=sQuery(id+"F0.wireOp",EDGE,"E25.0");var subQ6=sQuery(id+"F0.wireOp",EDGE,"E25.2");var subQ7=sQuery(id+"F0.wireOp",EDGE,"E25.3");Q4=makeQuery(id+"F8.boolean.opBoolean","INTERSECT",EDGE,{"derivedFrom":[makeQuery(id+"F5.boolean.opBoolean","SPLIT",FACE,{"disambiguationData":[TD([makeQuery(id+"F2.opExtrude","SWEPT_FACE",FACE,{"disambiguationData":[OSD([subQ5])]})])],"derivedFrom":makeQuery(id+"F3.boolean.opBoolean","COPY",FACE,{"derivedFrom":makeQuery(id+"F3.opExtrude","CAP_FACE",FACE,{"disambiguationData":[OSD([subQ5,subQ1,subQ6,subQ7,subQ4,subQ3,subQ2,subQ0])],"isStart":false})})}),makeQuery(id+"F8.opExtrude","SWEPT_FACE",FACE,{"disambiguationData":[OSD([sQuery(id+"F7.wireOp",EDGE,"E67")])]})]});}
            var Q5;
            Q5=makeQuery(id+"F8.boolean.opBoolean","INTERSECT",EDGE,{"disambiguationData":[OD(0.0)],"derivedFrom":[makeQuery(id+"F5.opExtrude","SWEPT_FACE",FACE,{"disambiguationData":[OSD([sQuery(id+"F4.wireOp",EDGE,"E30")])]}),makeQuery(id+"F8.opExtrude","SWEPT_FACE",FACE,{"disambiguationData":[OSD([sQuery(id+"F7.wireOp",EDGE,"E67")])]})]});
            fillet(context, id + "F14", {"entities" : qUnion([Q0, Q1, Q2, Q3, Q4, Q5]), "radius" : 3 * mm, "tangentPropagation" : true, "allowEdgeOverflow" : false});
        }
        {
            var Q0;
            Q0=makeQuery(id+"F1.opExtrude","CAP_EDGE",EDGE,{"disambiguationData":[OSD([sQuery(id+"F0.wireOp",EDGE,"E1.bottom")])],"isStart":false});
            fillet(context, id + "F15", {"entities" : qUnion([Q0]), "radius" : 2 * mm, "tangentPropagation" : true, "allowEdgeOverflow" : false});
        }
        {
            var Q0;
            {var subQ0=sQuery(id+"F0.wireOp",EDGE,"E21.filletArc");var subQ1=sQuery(id+"F0.wireOp",EDGE,"E7");var subQ2=sQuery(id+"F0.wireOp",EDGE,"E6");var subQ3=sQuery(id+"F0.wireOp",EDGE,"E5");var subQ4=sQuery(id+"F0.wireOp",EDGE,"E4");var subQ5=sQuery(id+"F0.wireOp",EDGE,"E22.filletArc");var subQ6=sQuery(id+"F0.wireOp",EDGE,"E1.bottom");var subQ7=sQuery(id+"F0.wireOp",EDGE,"E1.right");var subQ8=sQuery(id+"F0.wireOp",EDGE,"E1.top");var subQ9=sQuery(id+"F0.wireOp",EDGE,"E1.left");var subQ10=sQuery(id+"F0.wireOp",EDGE,"E23.filletArc");var subQ11=sQuery(id+"F0.wireOp",EDGE,"E24.filletArc");Q0=makeQuery(id+"F2.boolean.opBoolean","SPLIT",FACE,{"disambiguationData":[TD([makeQuery(id+"F1.opExtrude","SWEPT_FACE",FACE,{"disambiguationData":[OSD([subQ6])]})])],"derivedFrom":makeQuery(id+"F1.opExtrude","CAP_FACE",FACE,{"disambiguationData":[OSD([subQ6,subQ8,subQ9,subQ7,subQ4,subQ3,subQ2,subQ1,subQ0,subQ5,subQ10,subQ11])],"isStart":true})});}
            var sketch = newSketch(context, id + "F16", { "sketchPlane" : qUnion([Q0])});
            skLineSegment(sketch, "E79", {"start": v(-31.43, 74.25) * mm, "end": v(-13.2, 92.25) * mm});
            skLineSegment(sketch, "E80", {"start": v(34.8, 74.25) * mm, "end": v(16.8, 92.25) * mm});
            skLineSegment(sketch, "E81", {"start": v(-13.2, 92.25) * mm, "end": v(-13.2, 104.25) * mm});
            skLineSegment(sketch, "E82", {"start": v(16.8, 92.25) * mm, "end": v(16.8, 104.25) * mm});
            skArc(sketch, "E83", {"start": v(16.8, 104.25) * mm, "mid": v(1.8, 119.25) * mm, "end": v(-13.2, 104.25) * mm});
            skCircle(sketch, "E84", {"center": v(1.8, 104.25) * mm, "radius": 6 * mm});
            skLineSegment(sketch, "E85", {"start": v(1.8, 104.25) * mm, "end": v(1.8, 74.25) * mm, "construction": true});
            skLineSegment(sketch, "E86.MirrorCS", {"start": v(34.8, -74.25) * mm, "end": v(16.8, -92.25) * mm});
            skLineSegment(sketch, "E87.MirrorCS", {"start": v(-31.43, -74.25) * mm, "end": v(-13.2, -92.25) * mm});
            skLineSegment(sketch, "E88.MirrorCS", {"start": v(-13.2, -92.25) * mm, "end": v(-13.2, -104.25) * mm});
            skArc(sketch, "E89.MirrorCS", {"start": v(16.8, -104.25) * mm, "mid": v(1.8, -119.25) * mm, "end": v(-13.2, -104.25) * mm});
            skLineSegment(sketch, "E90.MirrorCS", {"start": v(16.8, -92.25) * mm, "end": v(16.8, -104.25) * mm});
            skCircle(sketch, "E91.MirrorC", {"center": v(1.8, -104.25) * mm, "radius": 6 * mm});
            skLineSegment(sketch, "E92.MirrorCS", {"start": v(1.8, -104.25) * mm, "end": v(1.8, -74.25) * mm, "construction": true});
            skLineSegment(sketch, "E93", {"start": v(-31.43, 74.25) * mm, "end": v(34.8, 74.25) * mm, "construction": true});
            skLineSegment(sketch, "E94", {"start": v(-31.43, -74.25) * mm, "end": v(34.8, -74.25) * mm, "construction": true});
            skSolve(sketch);
        }
        {
            var Q0;
            {var subQ0=sQuery(id+"F16.wireOp",EDGE,"E79");Q0=makeQuery(id+"F16.imprint","IMPRINT",FACE,{"disambiguationData":[TD([[makeQuery(id+"F16.imprint","IMPRINT",EDGE,{"derivedFrom":subQ0}),-1.0]])]});}
            var Q1;
            {var subQ1=sQuery(id+"F16.wireOp",EDGE,"E86.MirrorCS");Q1=makeQuery(id+"F16.imprint","IMPRINT",FACE,{"disambiguationData":[TD([[makeQuery(id+"F16.imprint","IMPRINT",EDGE,{"derivedFrom":subQ1}),-1.0]])]});}
            var Q2;
            Q2=makeQuery(id+"F2.opExtrude","CAP_FACE",FACE,{"disambiguationData":[OSD([sQuery(id+"F0.wireOp",EDGE,"E12"),sQuery(id+"F0.wireOp",EDGE,"E13"),sQuery(id+"F0.wireOp",EDGE,"E14"),sQuery(id+"F0.wireOp",EDGE,"E15"),sQuery(id+"F0.wireOp",EDGE,"E17.filletArc"),sQuery(id+"F0.wireOp",EDGE,"E18.filletArc"),sQuery(id+"F0.wireOp",EDGE,"E19.filletArc"),sQuery(id+"F0.wireOp",EDGE,"E20.filletArc"),sQuery(id+"F0.wireOp",EDGE,"E25.0"),sQuery(id+"F0.wireOp",EDGE,"E25.1"),sQuery(id+"F0.wireOp",EDGE,"E25.2"),sQuery(id+"F0.wireOp",EDGE,"E25.3"),sQuery(id+"F0.wireOp",EDGE,"E25.4"),sQuery(id+"F0.wireOp",EDGE,"E25.5"),sQuery(id+"F0.wireOp",EDGE,"E25.6"),sQuery(id+"F0.wireOp",EDGE,"E25.7")])],"isStart":false});
            extrude(context, id + "F17", {"entities" : qUnion([Q0, Q1]), "endBound" : BoundingType.UP_TO_SURFACE, "endBoundEntityFace" : qUnion([Q2]), "depth" : 25 * mm});
        }
    });
